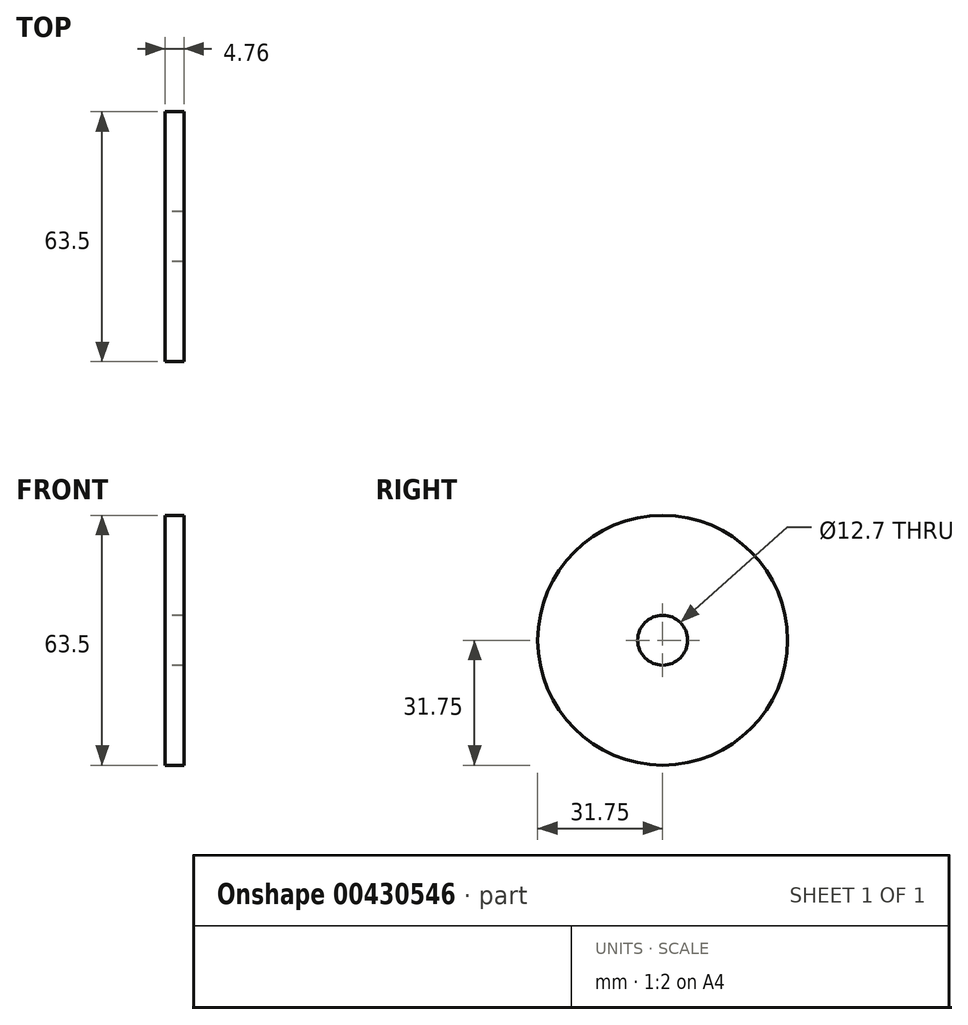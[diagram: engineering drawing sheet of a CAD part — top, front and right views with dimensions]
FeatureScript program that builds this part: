
annotation { "Feature Type Name" : "Feature", "Feature Type Description" : "" }
export const myFeature = defineFeature(function(context is Context, id is Id, definition is map)
    precondition{}
    {
        {
            var Q0;
            Q0=qCreatedBy(makeId("Right.planeOp"),FACE);
            var sketch = newSketch(context, id + "F0", { "sketchPlane" : qUnion([Q0])});
            skCircle(sketch, "E0", {"center": v(0, 0) * mm, "radius": 6.35 * mm});
            skCircle(sketch, "E1", {"center": v(0, 0) * mm, "radius": 31.75 * mm});
            skSolve(sketch);
        }
        {
            var Q0;
            Q0=makeQuery(id+"F0.imprint","IMPRINT",FACE,{"disambiguationData":[TD([[makeQuery(id+"F0.imprint","IMPRINT",EDGE,{"derivedFrom":sQuery(id+"F0.wireOp",EDGE,"E0")}),-1.0]])]});
            extrude(context, id + "F1", {"entities" : qUnion([Q0]), "depth" : 4.76 * mm});
        }
    });
